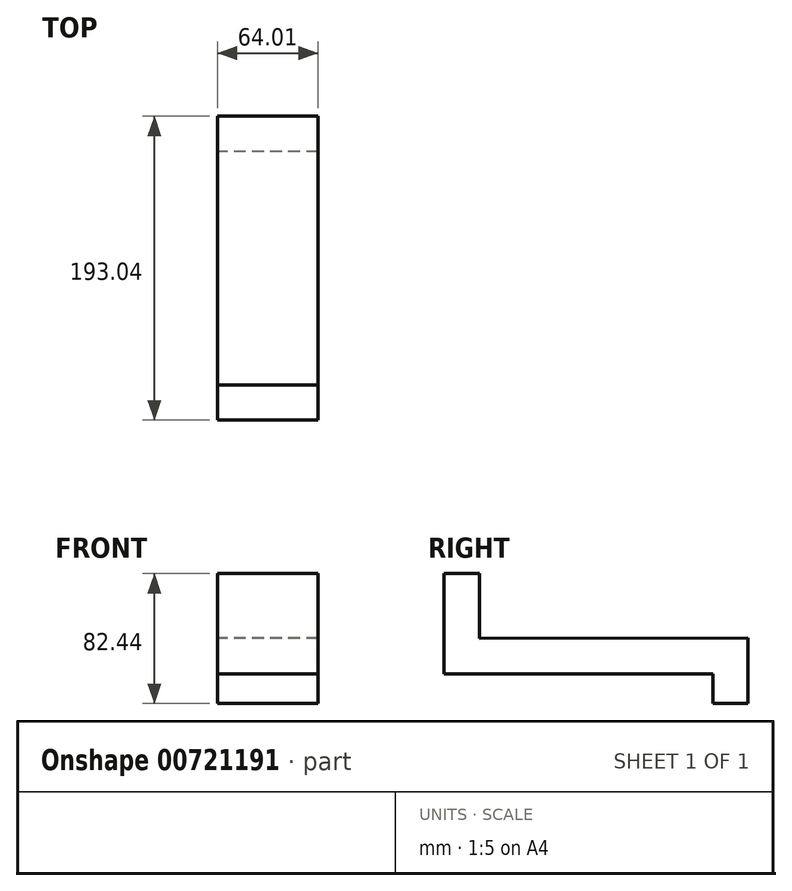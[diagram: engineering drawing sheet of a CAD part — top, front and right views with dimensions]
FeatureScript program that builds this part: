
annotation { "Feature Type Name" : "Feature", "Feature Type Description" : "" }
export const myFeature = defineFeature(function(context is Context, id is Id, definition is map)
    precondition{}
    {
        {
            var Q0;
            Q0=qCreatedBy(makeId("Right.planeOp"),FACE);
            var sketch = newSketch(context, id + "F0", { "sketchPlane" : qUnion([Q0])});
            skLineSegment(sketch, "E0", {"start": v(-68.32, 35.82) * mm, "end": v(-45.98, 35.82) * mm});
            skLineSegment(sketch, "E1", {"start": v(-68.32, 35.82) * mm, "end": v(-68.32, -27.82) * mm});
            skLineSegment(sketch, "E2", {"start": v(-68.32, -27.82) * mm, "end": v(102.37, -27.82) * mm});
            skLineSegment(sketch, "E3", {"start": v(102.37, -27.82) * mm, "end": v(102.37, -46.62) * mm});
            skLineSegment(sketch, "E4", {"start": v(102.37, -46.62) * mm, "end": v(124.72, -46.62) * mm});
            skLineSegment(sketch, "E5", {"start": v(124.72, -46.62) * mm, "end": v(124.72, -5.07) * mm});
            skLineSegment(sketch, "E6", {"start": v(-45.98, 35.82) * mm, "end": v(-45.98, -5.33) * mm});
            skLineSegment(sketch, "E7", {"start": v(124.72, -5.07) * mm, "end": v(-45.98, -5.33) * mm});
            skSolve(sketch);
        }
        {
            var Q0;
            Q0=makeQuery(id+"F0.imprint","IMPRINT",FACE,{"disambiguationData":[TD([[makeQuery(id+"F0.imprint","IMPRINT",EDGE,{"derivedFrom":sQuery(id+"F0.wireOp",EDGE,"E0")}),-1.0]])]});
            extrude(context, id + "F1", {"entities" : qUnion([Q0]), "depth" : 64 * mm, "offsetDistance" : 25.4 * mm});
        }
    });
